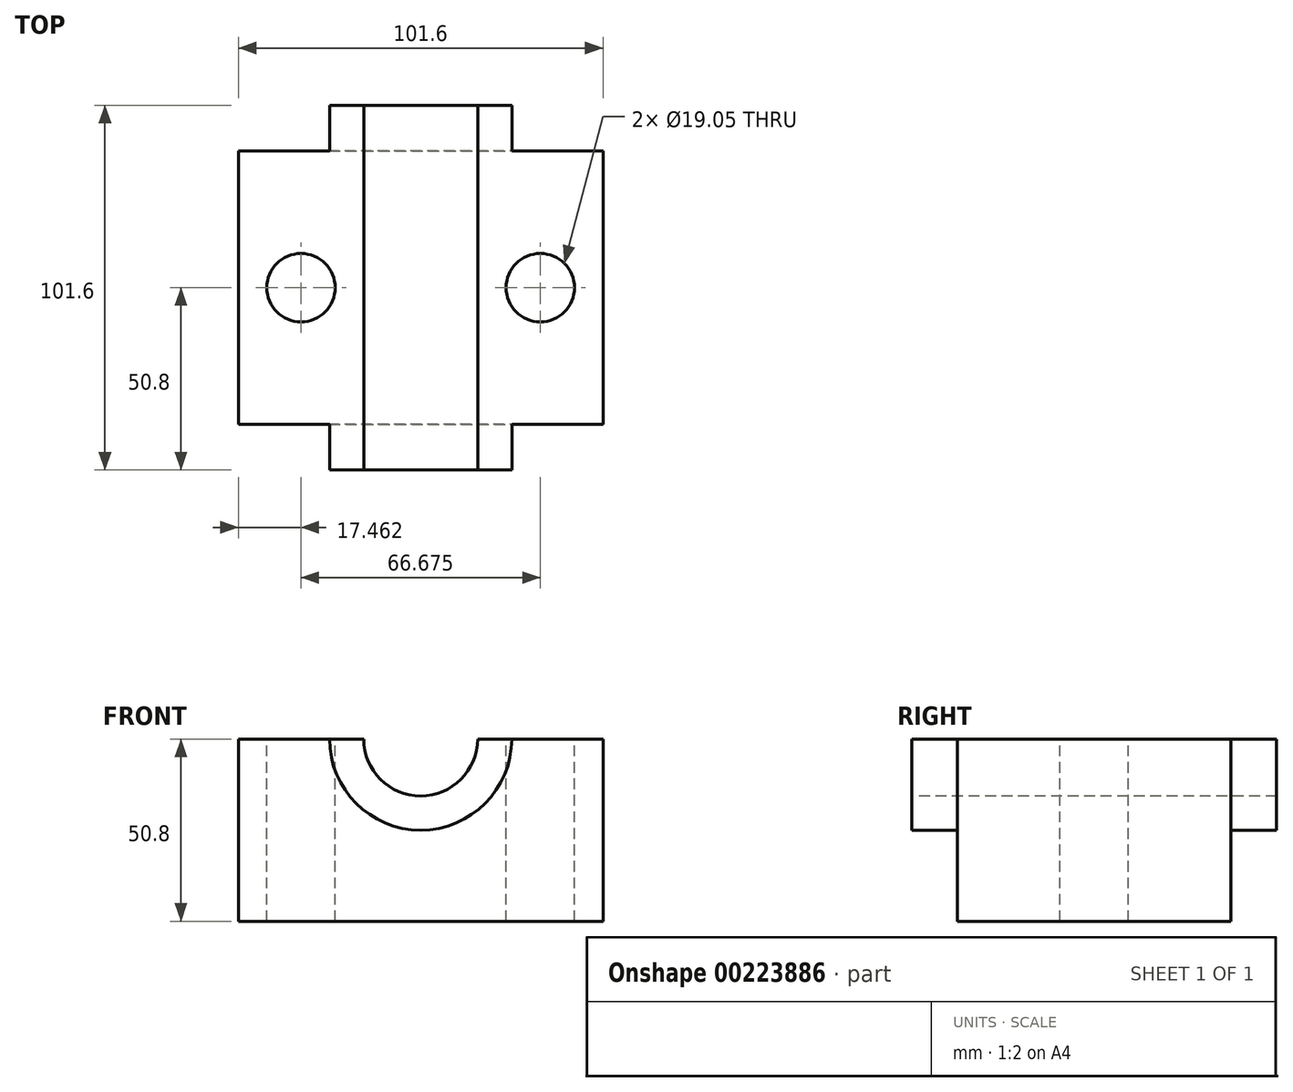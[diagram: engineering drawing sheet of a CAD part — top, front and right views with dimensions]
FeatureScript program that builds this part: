
annotation { "Feature Type Name" : "Feature", "Feature Type Description" : "" }
export const myFeature = defineFeature(function(context is Context, id is Id, definition is map)
    precondition{}
    {
        {
            var Q0;
            Q0=qCreatedBy(makeId("Top.planeOp"),FACE);
            var sketch = newSketch(context, id + "F0", { "sketchPlane" : qUnion([Q0])});
            skLineSegment(sketch, "E0.bottom", {"start": v(50.8, -38.1) * mm, "end": v(-50.8, -38.1) * mm});
            skLineSegment(sketch, "E0.top", {"start": v(50.8, 38.1) * mm, "end": v(-50.8, 38.1) * mm});
            skLineSegment(sketch, "E0.left", {"start": v(50.8, -38.1) * mm, "end": v(50.8, 38.1) * mm});
            skLineSegment(sketch, "E0.right", {"start": v(-50.8, -38.1) * mm, "end": v(-50.8, 38.1) * mm});
            skPoint(sketch, "E0.middle", {"position": v(0, 0) * mm});
            skSolve(sketch);
        }
        {
            var Q0;
            Q0 = qSketchRegion(id + "F0", true);
            extrude(context, id + "F1", {"entities" : qUnion([Q0]), "depth" : 50.8 * mm});
        }
        {
            var Q0;
            Q0=makeQuery(id+"F1.opExtrude","SWEPT_FACE",FACE,{"disambiguationData":[OSD([sQuery(id+"F0.wireOp",EDGE,"E0.bottom")])]});
            var sketch = newSketch(context, id + "F2", { "sketchPlane" : qUnion([Q0])});
            skArc(sketch, "E1", {"start": v(-25.4, 50.8) * mm, "mid": v(0, 25.4) * mm, "end": v(25.4, 50.8) * mm});
            skLineSegment(sketch, "E2", {"start": v(-25.4, 50.8) * mm, "end": v(25.4, 50.8) * mm});
            skSolve(sketch);
        }
        {
            var Q0;
            Q0 = qSketchRegion(id + "F2", true);
            extrude(context, id + "F3", {"entities" : qUnion([Q0]), "operationType" : NewBodyOperationType.ADD, "depth" : 12.7 * mm, "hasSecondDirection" : true, "secondDirectionOppositeDirection" : true, "secondDirectionDepth" : 88.9 * mm});
        }
        {
            var Q0;
            Q0=makeQuery(id+"F3.opExtrude","CAP_FACE",FACE,{"disambiguationData":[OSD([sQuery(id+"F2.wireOp",EDGE,"E1"),sQuery(id+"F2.wireOp",EDGE,"E2")])],"isStart":false});
            var sketch = newSketch(context, id + "F4", { "sketchPlane" : qUnion([Q0])});
            skCircle(sketch, "E3", {"center": v(0, 50.8) * mm, "radius": 15.88 * mm});
            skSolve(sketch);
        }
        {
            var Q0;
            Q0 = qSketchRegion(id + "F4", true);
            extrude(context, id + "F5", {"entities" : qUnion([Q0]), "operationType" : NewBodyOperationType.REMOVE, "oppositeDirection" : true, "depth" : 122.94 * mm});
        }
        {
            var Q0;
            {var subQ0=sQuery(id+"F0.wireOp",EDGE,"E0.right");var subQ2=sQuery(id+"F0.wireOp",EDGE,"E0.top");var subQ3=sQuery(id+"F0.wireOp",EDGE,"E0.bottom");var subQ4=sQuery(id+"F2.wireOp",EDGE,"E2");Q0=makeQuery(id+"F5.boolean.opBoolean","SPLIT",FACE,{"disambiguationData":[TD([makeQuery(id+"F1.opExtrude","SWEPT_FACE",FACE,{"disambiguationData":[OSD([subQ0])]})])],"derivedFrom":makeQuery(id+"F3.boolean.opBoolean","MERGE",FACE,{"derivedFrom":[makeQuery(id+"F1.opExtrude","CAP_FACE",FACE,{"disambiguationData":[OSD([subQ3,subQ2,sQuery(id+"F0.wireOp",EDGE,"E0.left"),subQ0])],"isStart":false}),makeQuery(id+"F3.opExtrude","SWEPT_FACE",FACE,{"disambiguationData":[OSD([subQ4])]})]})});}
            var sketch = newSketch(context, id + "F6", { "sketchPlane" : qUnion([Q0])});
            skCircle(sketch, "E4", {"center": v(-33.34, 0) * mm, "radius": 9.53 * mm});
            skPoint(sketch, "E4.centerSnap0", {"position": v(-33.34, 0) * mm});
            skSolve(sketch);
        }
        {
            var Q0;
            Q0=makeQuery(id+"F6.imprint","IMPRINT",FACE,{"disambiguationData":[TD([[makeQuery(id+"F6.imprint","IMPRINT",EDGE,{"derivedFrom":sQuery(id+"F6.wireOp",EDGE,"E4")}),1.0]])]});
            extrude(context, id + "F7", {"entities" : qUnion([Q0]), "operationType" : NewBodyOperationType.REMOVE, "oppositeDirection" : true, "depth" : 135.64 * mm});
        }
        {
            var Q0;
            {var subQ0=sQuery(id+"F0.wireOp",EDGE,"E0.left");var subQ1=sQuery(id+"F2.wireOp",EDGE,"E2");var subQ3=sQuery(id+"F0.wireOp",EDGE,"E0.top");var subQ4=sQuery(id+"F0.wireOp",EDGE,"E0.bottom");Q0=makeQuery(id+"F5.boolean.opBoolean","SPLIT",FACE,{"disambiguationData":[TD([makeQuery(id+"F1.opExtrude","SWEPT_FACE",FACE,{"disambiguationData":[OSD([subQ0])]})])],"derivedFrom":makeQuery(id+"F3.boolean.opBoolean","MERGE",FACE,{"derivedFrom":[makeQuery(id+"F1.opExtrude","CAP_FACE",FACE,{"disambiguationData":[OSD([subQ4,subQ3,subQ0,sQuery(id+"F0.wireOp",EDGE,"E0.right")])],"isStart":false}),makeQuery(id+"F3.opExtrude","SWEPT_FACE",FACE,{"disambiguationData":[OSD([subQ1])]})]})});}
            var sketch = newSketch(context, id + "F8", { "sketchPlane" : qUnion([Q0])});
            skCircle(sketch, "E5", {"center": v(33.34, 0) * mm, "radius": 9.53 * mm});
            skSolve(sketch);
        }
        {
            var Q0;
            Q0 = qSketchRegion(id + "F8", true);
            extrude(context, id + "F9", {"entities" : qUnion([Q0]), "operationType" : NewBodyOperationType.REMOVE, "oppositeDirection" : true, "depth" : 98.3 * mm});
        }
    });
